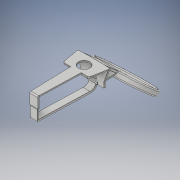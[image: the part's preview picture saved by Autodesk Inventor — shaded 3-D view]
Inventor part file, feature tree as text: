
AUTODESK INVENTOR PART (.ipt)
format: ipt  version: 2017 (Build 210142000, 142)  size: 1,438,208 bytes
history: native  units: mm
features: extrude x10, sketch x10, fillet x9, other x2, plane x1
ambient origin geometry x8: Origin, YZ Plane, XZ Plane, XY Plane, X Axis, Y Axis, Z Axis, Center Point
bodies: Body1 (feature_tree)
feature tree (32):
  extrude  "Extrusion2"  Depth=2.5mm TaperAngle=0.0deg
  extrude  "Extrusion3"  Depth=12.391838mm
  extrude  "Extrusion5"  Depth=28.099801mm
  plane  "Work Plane1"
  extrude  "Extrusion6"  Depth=6.5mm
  extrude  "Extrusion7"  Depth=3.5mm TaperAngle=0.0deg
  extrude  "Extrusion8"  Depth=2.5mm TaperAngle=0.0deg
  extrude  "Extrusion9"  Depth=2.5mm
  extrude  "Extrusion10"  Depth=2.5mm
  extrude  "Extrusion11"  Depth=22.863813mm
  fillet  "Fillet1"  Radius=4.0mm
  fillet  "Fillet3"  Radius=38.0mm
  fillet  "Fillet4"  Radius=10.0mm
  fillet  "Fillet5"  Radius=10.0mm
  fillet  "Fillet6"  Radius=1.4mm
  extrude  "Extrusion13"  Depth=2.0mm
  fillet  "Fillet8"  [1 undecoded]
  fillet  "Fillet9"  Radius=0.45mm
  fillet  "Fillet10"  Radius=2.0mm
  fillet  "Fillet11"  Radius=0.5mm
  sketch  "sketch1 - front_main"  dims[d66=26.0mm d67=12.391838mm]
  other  "Image1"
  sketch  "sketch2 - bottom_front_tab"  dims[d68=26.0mm d69=28.099801mm]
  sketch  "sketch3 - top_tab"  dims[d70=9.0mm d73=6.5mm]
  other  "Image2"
  sketch  "sketch5 - bottom_hinge"  dims[d74=6.5mm d76=3.5mm d77=0.0mm]
  sketch  "sketch6 - hinge_part"  dims[d82=17.0mm d88=2.5mm d89=0.0mm]
  sketch  "sketch7 - drink_arm"  dims[d90=12.789mm d91=0.0mm d92=2.5mm]
  sketch  "sketch8 - support_arm_arc_hole"  dims[d94=4.6mm d95=2.5mm]
  sketch  "sketch9 - cup_holder"  dims[d96=3.5mm d97=0.0mm d98=22.863813mm d99=4.0mm d100=38.0mm d101=0.0mm d106=10.0mm d107=0.0mm d109=10.0mm d110=0.0mm d111=1.4mm]
  sketch  "Sketch13"  dims[d12=2.5mm d13=0.0mm d18=2.5mm d19=0.0mm]
  sketch  "sketch4 - xbox_hole"  dims[d113=0.4mm d118=20.0mm d119=90.0deg d120=0.45mm d121=2.0mm d122=0.5mm d125=3.0mm d126=0.0mm d128=0.45mm d129=0.45mm d130=4.0mm d131=2.0mm]
note: 1 required parameter value undecoded (feature->parameter linkage not recoverable at this tier; creation-order binding heuristic only, values carry confidence <= 0.55)
